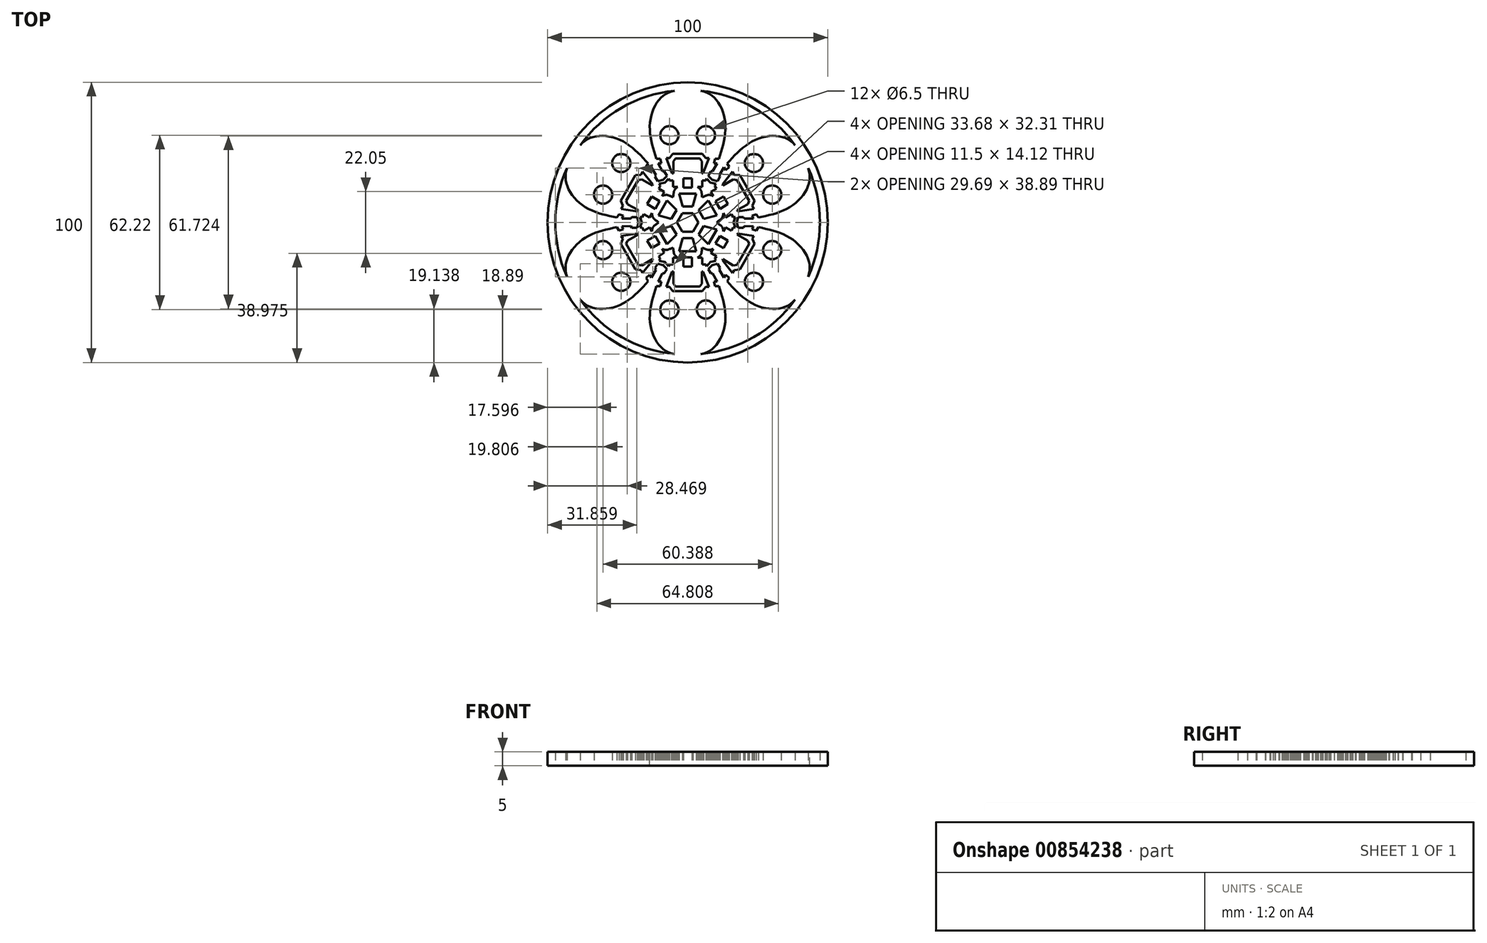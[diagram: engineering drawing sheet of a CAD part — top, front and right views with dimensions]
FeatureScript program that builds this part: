
annotation { "Feature Type Name" : "Feature", "Feature Type Description" : "" }
export const myFeature = defineFeature(function(context is Context, id is Id, definition is map)
    precondition{}
    {
        {
            var Q0;
            Q0=qCreatedBy(makeId("Top.planeOp"),FACE);
            var sketch = newSketch(context, id + "F0", { "sketchPlane" : qUnion([Q0])});
            skLineSegment(sketch, "E0", {"start": v(0, 0) * mm, "end": v(0, 50) * mm});
            skLineSegment(sketch, "E1.1.0", {"start": v(0, 0) * mm, "end": v(-25, 43.3) * mm});
            skLineSegment(sketch, "E1.2.0", {"start": v(0, 0) * mm, "end": v(-43.3, 25) * mm});
            skLineSegment(sketch, "E1.3.0", {"start": v(0, 0) * mm, "end": v(-50, 0) * mm});
            skLineSegment(sketch, "E1.4.0", {"start": v(0, 0) * mm, "end": v(-43.3, -25) * mm});
            skLineSegment(sketch, "E1.5.0", {"start": v(0, 0) * mm, "end": v(-25, -43.3) * mm});
            skLineSegment(sketch, "E1.6.0", {"start": v(0, 0) * mm, "end": v(0, -50) * mm});
            skLineSegment(sketch, "E1.7.0", {"start": v(0, 0) * mm, "end": v(25, -43.3) * mm});
            skLineSegment(sketch, "E1.8.0", {"start": v(0, 0) * mm, "end": v(43.3, -25) * mm});
            skLineSegment(sketch, "E1.9.0", {"start": v(0, 0) * mm, "end": v(50, 0) * mm});
            skLineSegment(sketch, "E1.10.0", {"start": v(0, 0) * mm, "end": v(43.3, 25) * mm});
            skLineSegment(sketch, "E1.11.0", {"start": v(0, 0) * mm, "end": v(25, 43.3) * mm});
            skPoint(sketch, "E1.center", {"position": v(0, 0) * mm});
            skFitSpline(sketch, "E2", {"points": [v(0, 47.42) * mm, v(-9.45, 44.59) * mm, v(-13.5, 34.9) * mm, v(-11.14, 22.73) * mm], "startDerivative": vector(-39.84, 0.36) * mm, "endDerivative": vector(11.08, -33.07) * mm});
            skLineSegment(sketch, "E3", {"start": v(-11.14, 22.73) * mm, "end": v(-9.73, 22.73) * mm});
            skLineSegment(sketch, "E4", {"start": v(-9.73, 22.73) * mm, "end": v(-9.36, 21.09) * mm});
            skLineSegment(sketch, "E5", {"start": v(-9.36, 21.09) * mm, "end": v(-10.54, 21.09) * mm});
            skLineSegment(sketch, "E6", {"start": v(-10.54, 21.09) * mm, "end": v(-8.96, 18.21) * mm});
            skLineSegment(sketch, "E7", {"start": v(-8.96, 18.21) * mm, "end": v(-8.32, 18.21) * mm});
            skLineSegment(sketch, "E8", {"start": v(-8.32, 18.21) * mm, "end": v(-7.4, 16.6) * mm});
            skCircle(sketch, "E9", {"center": v(-6.5, 31.1) * mm, "radius": 3.25 * mm});
            skLineSegment(sketch, "E10", {"start": v(-7.4, 16.6) * mm, "end": v(-8.78, 15.2) * mm});
            skLineSegment(sketch, "E11", {"start": v(-8.18, 14.16) * mm, "end": v(-6.89, 15.63) * mm});
            skLineSegment(sketch, "E12", {"start": v(-6.89, 15.63) * mm, "end": v(-6.5, 14.97) * mm});
            skLineSegment(sketch, "E13", {"start": v(-6.5, 14.97) * mm, "end": v(-5.25, 14.97) * mm});
            skLineSegment(sketch, "E14", {"start": v(-5.25, 14.97) * mm, "end": v(-5.25, 12.64) * mm});
            skLineSegment(sketch, "E15", {"start": v(-5.25, 12.64) * mm, "end": v(-3.55, 12.64) * mm});
            skPoint(sketch, "E16.2.internal.snap0", {"position": v(-5.25, 13.8) * mm});
            skLineSegment(sketch, "E17", {"start": v(-1.89, 3.27) * mm, "end": v(0, 3.27) * mm});
            skLineSegment(sketch, "E18", {"start": v(0, 5.63) * mm, "end": v(-1.8, 5.63) * mm});
            skLineSegment(sketch, "E19", {"start": v(-1.8, 5.63) * mm, "end": v(-3.05, 10.3) * mm});
            skLineSegment(sketch, "E20", {"start": v(-3.05, 10.3) * mm, "end": v(0, 10.3) * mm});
            skFitSpline(sketch, "E21", {"points": [v(-3.55, 12.64) * mm, v(-4.78, 11.36) * mm, v(-5.2, 9) * mm], "startDerivative": vector(-4.82, -3.1) * mm, "endDerivative": vector(-1.27, -9.2) * mm});
            skLineSegment(sketch, "E22", {"start": v(0, 12.43) * mm, "end": v(-1.56, 12.43) * mm});
            skLineSegment(sketch, "E23", {"start": v(-1.56, 12.43) * mm, "end": v(-1.56, 15.75) * mm});
            skLineSegment(sketch, "E24", {"start": v(-1.56, 15.75) * mm, "end": v(0, 15.75) * mm});
            skLineSegment(sketch, "E25", {"start": v(0, 24.54) * mm, "end": v(-5.27, 24.54) * mm});
            skLineSegment(sketch, "E26", {"start": v(-5.27, 24.54) * mm, "end": v(-6.44, 22.95) * mm});
            skLineSegment(sketch, "E27", {"start": v(-6.44, 22.95) * mm, "end": v(-7.63, 22.95) * mm});
            skLineSegment(sketch, "E28", {"start": v(-7.63, 22.95) * mm, "end": v(-5.52, 17.5) * mm});
            skLineSegment(sketch, "E29", {"start": v(-5.52, 17.5) * mm, "end": v(-5.06, 17.5) * mm});
            skLineSegment(sketch, "E30", {"start": v(-5.06, 17.5) * mm, "end": v(-5.13, 21.82) * mm});
            skLineSegment(sketch, "E31", {"start": v(-5.13, 21.82) * mm, "end": v(-4.3, 22.84) * mm});
            skLineSegment(sketch, "E32", {"start": v(-4.3, 22.84) * mm, "end": v(0, 22.84) * mm});
            skLineSegment(sketch, "E33.MirrorCS", {"start": v(6.5, 14.97) * mm, "end": v(5.25, 14.97) * mm});
            skLineSegment(sketch, "E34.MirrorCS", {"start": v(5.25, 14.97) * mm, "end": v(5.25, 12.64) * mm});
            skLineSegment(sketch, "E35.MirrorCS", {"start": v(5.25, 12.64) * mm, "end": v(3.55, 12.64) * mm});
            skLineSegment(sketch, "E36.MirrorCS", {"start": v(9.36, 21.09) * mm, "end": v(10.54, 21.09) * mm});
            skLineSegment(sketch, "E37.MirrorCS", {"start": v(10.54, 21.09) * mm, "end": v(8.96, 18.21) * mm});
            skLineSegment(sketch, "E38.MirrorCS", {"start": v(6.89, 15.63) * mm, "end": v(6.5, 14.97) * mm});
            skLineSegment(sketch, "E39.MirrorCS", {"start": v(8.96, 18.21) * mm, "end": v(8.32, 18.21) * mm});
            skLineSegment(sketch, "E40.MirrorCS", {"start": v(8.32, 18.21) * mm, "end": v(7.4, 16.6) * mm});
            skLineSegment(sketch, "E41.MirrorCS", {"start": v(7.4, 16.6) * mm, "end": v(8.78, 15.2) * mm});
            skFitSpline(sketch, "E42.MirrorCS", {"points": [v(3.55, 12.64) * mm, v(4.78, 11.36) * mm, v(5.2, 9) * mm], "startDerivative": vector(4.82, -3.1) * mm, "endDerivative": vector(1.27, -9.2) * mm});
            skLineSegment(sketch, "E43.MirrorCS", {"start": v(6.44, 22.95) * mm, "end": v(7.63, 22.95) * mm});
            skLineSegment(sketch, "E44.MirrorCS", {"start": v(5.52, 17.5) * mm, "end": v(5.06, 17.5) * mm});
            skLineSegment(sketch, "E45.MirrorCS", {"start": v(11.14, 22.73) * mm, "end": v(9.73, 22.73) * mm});
            skLineSegment(sketch, "E46.MirrorCS", {"start": v(8.18, 14.16) * mm, "end": v(6.89, 15.63) * mm});
            skLineSegment(sketch, "E47.MirrorCS", {"start": v(9.73, 22.73) * mm, "end": v(9.36, 21.09) * mm});
            skLineSegment(sketch, "E48.MirrorCS", {"start": v(5.27, 24.54) * mm, "end": v(6.44, 22.95) * mm});
            skLineSegment(sketch, "E49.MirrorCS", {"start": v(1.8, 5.63) * mm, "end": v(3.05, 10.3) * mm});
            skLineSegment(sketch, "E50.MirrorCS", {"start": v(5.06, 17.5) * mm, "end": v(5.13, 21.82) * mm});
            skLineSegment(sketch, "E51.MirrorCS", {"start": v(7.63, 22.95) * mm, "end": v(5.52, 17.5) * mm});
            skLineSegment(sketch, "E52.MirrorCS", {"start": v(5.13, 21.82) * mm, "end": v(4.3, 22.84) * mm});
            skLineSegment(sketch, "E53.MirrorCS", {"start": v(1.56, 12.43) * mm, "end": v(1.56, 15.75) * mm});
            skPoint(sketch, "E54.MirrorP", {"position": v(5.25, 13.8) * mm});
            skCircle(sketch, "E55.MirrorC", {"center": v(6.5, 31.1) * mm, "radius": 3.25 * mm});
            skFitSpline(sketch, "E56.MirrorCS", {"points": [v(0, 47.42) * mm, v(9.45, 44.59) * mm, v(13.5, 34.9) * mm, v(11.14, 22.73) * mm], "startDerivative": vector(39.84, 0.36) * mm, "endDerivative": vector(-11.08, -33.07) * mm});
            skLineSegment(sketch, "E57.MirrorCS", {"start": v(0, 24.54) * mm, "end": v(5.27, 24.54) * mm});
            skLineSegment(sketch, "E58.MirrorCS", {"start": v(4.3, 22.84) * mm, "end": v(0, 22.84) * mm});
            skLineSegment(sketch, "E59.MirrorCS", {"start": v(1.56, 15.75) * mm, "end": v(0, 15.75) * mm});
            skLineSegment(sketch, "E60.MirrorCS", {"start": v(0, 12.43) * mm, "end": v(1.56, 12.43) * mm});
            skLineSegment(sketch, "E61.MirrorCS", {"start": v(3.05, 10.3) * mm, "end": v(0, 10.3) * mm});
            skLineSegment(sketch, "E62.MirrorCS", {"start": v(0, 5.63) * mm, "end": v(1.8, 5.63) * mm});
            skLineSegment(sketch, "E63.MirrorCS", {"start": v(1.89, 3.27) * mm, "end": v(0, 3.27) * mm});
            skLineSegment(sketch, "E64.MirrorCS", {"start": v(13.58, 1.77) * mm, "end": v(12.72, 3.25) * mm});
            skLineSegment(sketch, "E65.MirrorCS", {"start": v(8.32, 10.87) * mm, "end": v(9.18, 9.4) * mm});
            skLineSegment(sketch, "E66.MirrorCS", {"start": v(12.4, 13.53) * mm, "end": v(12.62, 13.13) * mm});
            skLineSegment(sketch, "E67.MirrorCS", {"start": v(10.76, 6.22) * mm, "end": v(9.98, 7.57) * mm});
            skFitSpline(sketch, "E68.MirrorCS", {"points": [v(9.18, 9.4) * mm, v(7.45, 9.82) * mm, v(5.2, 9) * mm], "startDerivative": vector(-5.1, 2.62) * mm, "endDerivative": vector(-8.6, -3.5) * mm});
            skLineSegment(sketch, "E69.MirrorCS", {"start": v(14.82, 19.8) * mm, "end": v(13.59, 18.65) * mm});
            skLineSegment(sketch, "E70.MirrorCS", {"start": v(15.59, 2.93) * mm, "end": v(13.58, 1.77) * mm});
            skLineSegment(sketch, "E71.MirrorCS", {"start": v(22.94, 2.44) * mm, "end": v(23.53, 1.42) * mm});
            skFitSpline(sketch, "E72.MirrorCS", {"points": [v(12.72, 3.25) * mm, v(12.23, 1.54) * mm, v(10.39, 0) * mm], "startDerivative": vector(-0.27, -5.72) * mm, "endDerivative": vector(-7.33, -5.7) * mm});
            skLineSegment(sketch, "E73.MirrorCS", {"start": v(16.21, 1.85) * mm, "end": v(15.59, 2.93) * mm});
            skLineSegment(sketch, "E74.MirrorCS", {"start": v(16.98, 1.85) * mm, "end": v(16.21, 1.85) * mm});
            skLineSegment(sketch, "E75.MirrorCS", {"start": v(14.12, 21.01) * mm, "end": v(14.82, 19.8) * mm});
            skLineSegment(sketch, "E76.MirrorCS", {"start": v(13.59, 18.65) * mm, "end": v(13, 19.67) * mm});
            skLineSegment(sketch, "E77.MirrorCS", {"start": v(25.25, 1.72) * mm, "end": v(24.55, 2.94) * mm});
            skLineSegment(sketch, "E78.MirrorCS", {"start": v(10.76, 6.22) * mm, "end": v(11.55, 4.86) * mm});
            skLineSegment(sketch, "E79.MirrorCS", {"start": v(17.91, 3.97) * mm, "end": v(17.68, 4.37) * mm});
            skLineSegment(sketch, "E80.MirrorCS", {"start": v(24.55, 2.94) * mm, "end": v(22.94, 2.44) * mm});
            skLineSegment(sketch, "E81.MirrorCS", {"start": v(13, 19.67) * mm, "end": v(11.3, 16.86) * mm});
            skLineSegment(sketch, "E82.MirrorCS", {"start": v(17.68, 4.37) * mm, "end": v(21.46, 6.46) * mm});
            skLineSegment(sketch, "E83.MirrorCS", {"start": v(10.45, 2.5) * mm, "end": v(8.92, 5.15) * mm});
            skLineSegment(sketch, "E84.MirrorCS", {"start": v(11.55, 4.86) * mm, "end": v(14.42, 6.52) * mm});
            skLineSegment(sketch, "E85.MirrorCS", {"start": v(4.88, 2.81) * mm, "end": v(5.78, 1.25) * mm});
            skLineSegment(sketch, "E86.MirrorCS", {"start": v(19.93, 1.9) * mm, "end": v(18.08, 1.9) * mm});
            skLineSegment(sketch, "E87.MirrorCS", {"start": v(23.1, 5.9) * mm, "end": v(23.69, 4.87) * mm});
            skLineSegment(sketch, "E88.MirrorCS", {"start": v(21.46, 6.46) * mm, "end": v(21.93, 7.7) * mm});
            skLineSegment(sketch, "E89.MirrorCS", {"start": v(16.35, 0) * mm, "end": v(16.98, 1.85) * mm});
            skLineSegment(sketch, "E90.MirrorCS", {"start": v(12.86, 9.23) * mm, "end": v(13.64, 7.88) * mm});
            skLineSegment(sketch, "E91.MirrorCS", {"start": v(11.61, 16.31) * mm, "end": v(10.69, 14.7) * mm});
            skLineSegment(sketch, "E92.MirrorCS", {"start": v(10.1, 13.78) * mm, "end": v(9.7, 13.12) * mm});
            skLineSegment(sketch, "E93.MirrorCS", {"start": v(14.42, 6.52) * mm, "end": v(13.64, 7.88) * mm});
            skLineSegment(sketch, "E94.MirrorCS", {"start": v(7.4, 7.8) * mm, "end": v(8.92, 5.15) * mm});
            skLineSegment(sketch, "E95.MirrorCS", {"start": v(9.98, 7.57) * mm, "end": v(12.86, 9.23) * mm});
            skLineSegment(sketch, "E96.MirrorCS", {"start": v(9.7, 13.12) * mm, "end": v(10.33, 12.03) * mm});
            skLineSegment(sketch, "E97.MirrorCS", {"start": v(4.88, 2.81) * mm, "end": v(3.97, 4.38) * mm});
            skLineSegment(sketch, "E98.MirrorCS", {"start": v(10.69, 14.7) * mm, "end": v(8.78, 15.2) * mm});
            skLineSegment(sketch, "E99.MirrorCS", {"start": v(21.25, 12.27) * mm, "end": v(23.89, 7.7) * mm});
            skLineSegment(sketch, "E100.MirrorCS", {"start": v(18.62, 16.84) * mm, "end": v(16.65, 17.05) * mm});
            skLineSegment(sketch, "E101.MirrorCS", {"start": v(16.06, 18.08) * mm, "end": v(12.4, 13.53) * mm});
            skLineSegment(sketch, "E102.MirrorCS", {"start": v(23.53, 1.42) * mm, "end": v(20.25, 1.35) * mm});
            skLineSegment(sketch, "E103.MirrorCS", {"start": v(16.33, 15.35) * mm, "end": v(17.64, 15.14) * mm});
            skLineSegment(sketch, "E104.MirrorCS", {"start": v(20.25, 1.35) * mm, "end": v(19.93, 1.9) * mm});
            skLineSegment(sketch, "E105.MirrorCS", {"start": v(23.89, 7.7) * mm, "end": v(23.1, 5.9) * mm});
            skLineSegment(sketch, "E106.MirrorCS", {"start": v(11.3, 16.86) * mm, "end": v(11.61, 16.31) * mm});
            skLineSegment(sketch, "E107.MirrorCS", {"start": v(8.18, 14.16) * mm, "end": v(10.1, 13.78) * mm});
            skLineSegment(sketch, "E108.MirrorCS", {"start": v(21.93, 7.7) * mm, "end": v(19.78, 11.42) * mm});
            skLineSegment(sketch, "E109.MirrorCS", {"start": v(12.62, 13.13) * mm, "end": v(16.33, 15.35) * mm});
            skLineSegment(sketch, "E110.MirrorCS", {"start": v(18.08, 1.9) * mm, "end": v(17.56, 0) * mm});
            skLineSegment(sketch, "E111.MirrorCS", {"start": v(10.33, 12.03) * mm, "end": v(8.32, 10.87) * mm});
            skLineSegment(sketch, "E112.MirrorCS", {"start": v(16.65, 17.05) * mm, "end": v(16.06, 18.08) * mm});
            skLineSegment(sketch, "E113.MirrorCS", {"start": v(3.77, 0) * mm, "end": v(2.83, 1.63) * mm});
            skLineSegment(sketch, "E114.MirrorCS", {"start": v(3.97, 4.38) * mm, "end": v(7.4, 7.8) * mm});
            skLineSegment(sketch, "E115.MirrorCS", {"start": v(1.89, 3.27) * mm, "end": v(2.83, 1.63) * mm});
            skLineSegment(sketch, "E116.MirrorCS", {"start": v(5.78, 1.25) * mm, "end": v(10.45, 2.5) * mm});
            skFitSpline(sketch, "E117.MirrorCS", {"points": [v(41.07, 23.71) * mm, v(43.34, 14.1) * mm, v(36.97, 5.76) * mm, v(25.25, 1.72) * mm], "startDerivative": vector(20.23, -34.33) * mm, "endDerivative": vector(-34.18, -6.94) * mm});
            skPoint(sketch, "E118.MirrorP", {"position": v(14.58, 2.35) * mm});
            skLineSegment(sketch, "E119.MirrorCS", {"start": v(21.25, 12.27) * mm, "end": v(18.62, 16.84) * mm});
            skPoint(sketch, "E120.MirrorP", {"position": v(9.33, 11.45) * mm});
            skLineSegment(sketch, "E121.MirrorCS", {"start": v(17.64, 15.14) * mm, "end": v(19.78, 11.42) * mm});
            skCircle(sketch, "E122.MirrorC", {"center": v(30.2, 9.92) * mm, "radius": 3.25 * mm});
            skLineSegment(sketch, "E123.MirrorCS", {"start": v(23.69, 4.87) * mm, "end": v(17.91, 3.97) * mm});
            skFitSpline(sketch, "E124.MirrorCS", {"points": [v(41.07, 23.71) * mm, v(33.89, 30.48) * mm, v(23.48, 29.14) * mm, v(14.12, 21.01) * mm], "startDerivative": vector(-19.61, 34.68) * mm, "endDerivative": vector(-23.1, -26.13) * mm});
            skCircle(sketch, "E125.MirrorC", {"center": v(23.69, 21.19) * mm, "radius": 3.25 * mm});
            skLineSegment(sketch, "E126.MirrorCS", {"start": v(-8.32, 10.87) * mm, "end": v(-9.18, 9.4) * mm});
            skLineSegment(sketch, "E127.MirrorCS", {"start": v(-19.93, -1.9) * mm, "end": v(-18.08, -1.9) * mm});
            skLineSegment(sketch, "E128.MirrorCS", {"start": v(-12.4, 13.53) * mm, "end": v(-12.62, 13.13) * mm});
            skLineSegment(sketch, "E129.MirrorCS", {"start": v(-8.32, -10.87) * mm, "end": v(-9.18, -9.4) * mm});
            skFitSpline(sketch, "E130.MirrorCS", {"points": [v(-12.72, -3.25) * mm, v(-12.23, -1.54) * mm, v(-10.39, 0) * mm], "startDerivative": vector(0.27, 5.72) * mm, "endDerivative": vector(7.33, 5.7) * mm});
            skLineSegment(sketch, "E131.MirrorCS", {"start": v(-13.58, 1.77) * mm, "end": v(-12.72, 3.25) * mm});
            skLineSegment(sketch, "E132.MirrorCS", {"start": v(-20.25, -1.35) * mm, "end": v(-19.93, -1.9) * mm});
            skFitSpline(sketch, "E133.MirrorCS", {"points": [v(-12.72, 3.25) * mm, v(-12.23, 1.54) * mm, v(-10.39, 0) * mm], "startDerivative": vector(0.27, -5.72) * mm, "endDerivative": vector(7.33, -5.7) * mm});
            skLineSegment(sketch, "E134.MirrorCS", {"start": v(-13.58, -1.77) * mm, "end": v(-12.72, -3.25) * mm});
            skLineSegment(sketch, "E135.MirrorCS", {"start": v(-16.98, -1.85) * mm, "end": v(-16.21, -1.85) * mm});
            skLineSegment(sketch, "E136.MirrorCS", {"start": v(-10.76, 6.22) * mm, "end": v(-11.55, 4.86) * mm});
            skLineSegment(sketch, "E137.MirrorCS", {"start": v(-10.1, -13.78) * mm, "end": v(-9.7, -13.12) * mm});
            skLineSegment(sketch, "E138.MirrorCS", {"start": v(-16.21, -1.85) * mm, "end": v(-15.59, -2.93) * mm});
            skLineSegment(sketch, "E139.MirrorCS", {"start": v(-25.25, -1.72) * mm, "end": v(-24.55, -2.94) * mm});
            skLineSegment(sketch, "E140.MirrorCS", {"start": v(-16.35, 0) * mm, "end": v(-16.98, -1.85) * mm});
            skLineSegment(sketch, "E141.MirrorCS", {"start": v(-18.08, 1.9) * mm, "end": v(-17.56, 0) * mm});
            skLineSegment(sketch, "E142.MirrorCS", {"start": v(-9.7, -13.12) * mm, "end": v(-10.33, -12.03) * mm});
            skLineSegment(sketch, "E143.MirrorCS", {"start": v(-14.12, -21.01) * mm, "end": v(-14.82, -19.8) * mm});
            skLineSegment(sketch, "E144.MirrorCS", {"start": v(-8.18, -14.16) * mm, "end": v(-10.1, -13.78) * mm});
            skFitSpline(sketch, "E145.MirrorCS", {"points": [v(-9.18, -9.4) * mm, v(-7.45, -9.82) * mm, v(-5.2, -9) * mm], "startDerivative": vector(5.1, -2.62) * mm, "endDerivative": vector(8.6, 3.5) * mm});
            skLineSegment(sketch, "E146.MirrorCS", {"start": v(-15.59, -2.93) * mm, "end": v(-13.58, -1.77) * mm});
            skLineSegment(sketch, "E147.MirrorCS", {"start": v(-10.1, 13.78) * mm, "end": v(-9.7, 13.12) * mm});
            skLineSegment(sketch, "E148.MirrorCS", {"start": v(-10.76, 6.22) * mm, "end": v(-9.98, 7.57) * mm});
            skLineSegment(sketch, "E149.MirrorCS", {"start": v(-16.98, 1.85) * mm, "end": v(-16.21, 1.85) * mm});
            skLineSegment(sketch, "E150.MirrorCS", {"start": v(-25.25, 1.72) * mm, "end": v(-24.55, 2.94) * mm});
            skLineSegment(sketch, "E151.MirrorCS", {"start": v(-16.35, 0) * mm, "end": v(-16.98, 1.85) * mm});
            skLineSegment(sketch, "E152.MirrorCS", {"start": v(-18.08, -1.9) * mm, "end": v(-17.56, 0) * mm});
            skLineSegment(sketch, "E153.MirrorCS", {"start": v(-9.7, 13.12) * mm, "end": v(-10.33, 12.03) * mm});
            skLineSegment(sketch, "E154.MirrorCS", {"start": v(-10.33, -12.03) * mm, "end": v(-8.32, -10.87) * mm});
            skLineSegment(sketch, "E155.MirrorCS", {"start": v(-13.59, -18.65) * mm, "end": v(-13, -19.67) * mm});
            skLineSegment(sketch, "E156.MirrorCS", {"start": v(-11.61, -16.31) * mm, "end": v(-10.69, -14.7) * mm});
            skLineSegment(sketch, "E157.MirrorCS", {"start": v(-10.76, -6.22) * mm, "end": v(-11.55, -4.86) * mm});
            skLineSegment(sketch, "E158.MirrorCS", {"start": v(-10.76, -6.22) * mm, "end": v(-9.98, -7.57) * mm});
            skLineSegment(sketch, "E159.MirrorCS", {"start": v(-15.59, 2.93) * mm, "end": v(-13.58, 1.77) * mm});
            skLineSegment(sketch, "E160.MirrorCS", {"start": v(-17.91, 3.97) * mm, "end": v(-17.68, 4.37) * mm});
            skLineSegment(sketch, "E161.MirrorCS", {"start": v(-10.69, -14.7) * mm, "end": v(-8.78, -15.2) * mm});
            skLineSegment(sketch, "E162.MirrorCS", {"start": v(-16.21, 1.85) * mm, "end": v(-15.59, 2.93) * mm});
            skLineSegment(sketch, "E163.MirrorCS", {"start": v(-8.18, 14.16) * mm, "end": v(-10.1, 13.78) * mm});
            skLineSegment(sketch, "E164.MirrorCS", {"start": v(-14.12, 21.01) * mm, "end": v(-14.82, 19.8) * mm});
            skFitSpline(sketch, "E165.MirrorCS", {"points": [v(-9.18, 9.4) * mm, v(-7.45, 9.82) * mm, v(-5.2, 9) * mm], "startDerivative": vector(5.1, 2.62) * mm, "endDerivative": vector(8.6, -3.5) * mm});
            skLineSegment(sketch, "E166.MirrorCS", {"start": v(-3.77, 0) * mm, "end": v(-2.83, -1.63) * mm});
            skLineSegment(sketch, "E167.MirrorCS", {"start": v(-1.89, -3.27) * mm, "end": v(-2.83, -1.63) * mm});
            skLineSegment(sketch, "E168.MirrorCS", {"start": v(-10.33, 12.03) * mm, "end": v(-8.32, 10.87) * mm});
            skLineSegment(sketch, "E169.MirrorCS", {"start": v(-13.59, 18.65) * mm, "end": v(-13, 19.67) * mm});
            skLineSegment(sketch, "E170.MirrorCS", {"start": v(-23.1, -5.9) * mm, "end": v(-23.69, -4.87) * mm});
            skLineSegment(sketch, "E171.MirrorCS", {"start": v(-14.42, 6.52) * mm, "end": v(-13.64, 7.88) * mm});
            skLineSegment(sketch, "E172.MirrorCS", {"start": v(-11.3, 16.86) * mm, "end": v(-11.61, 16.31) * mm});
            skLineSegment(sketch, "E173.MirrorCS", {"start": v(-10.45, 2.5) * mm, "end": v(-8.92, 5.15) * mm});
            skLineSegment(sketch, "E174.MirrorCS", {"start": v(-12.86, -9.23) * mm, "end": v(-13.64, -7.88) * mm});
            skLineSegment(sketch, "E175.MirrorCS", {"start": v(-17.68, -4.37) * mm, "end": v(-21.46, -6.46) * mm});
            skLineSegment(sketch, "E176.MirrorCS", {"start": v(-18.62, -16.84) * mm, "end": v(-16.65, -17.05) * mm});
            skLineSegment(sketch, "E177.MirrorCS", {"start": v(-10.69, 14.7) * mm, "end": v(-8.78, 15.2) * mm});
            skLineSegment(sketch, "E178.MirrorCS", {"start": v(-16.65, 17.05) * mm, "end": v(-16.06, 18.08) * mm});
            skLineSegment(sketch, "E179.MirrorCS", {"start": v(-9.98, 7.57) * mm, "end": v(-12.86, 9.23) * mm});
            skLineSegment(sketch, "E180.MirrorCS", {"start": v(-23.1, 5.9) * mm, "end": v(-23.69, 4.87) * mm});
            skLineSegment(sketch, "E181.MirrorCS", {"start": v(-20.25, 1.35) * mm, "end": v(-19.93, 1.9) * mm});
            skLineSegment(sketch, "E182.MirrorCS", {"start": v(-3.77, 0) * mm, "end": v(-2.83, 1.63) * mm});
            skLineSegment(sketch, "E183.MirrorCS", {"start": v(-12.4, -13.53) * mm, "end": v(-12.62, -13.13) * mm});
            skLineSegment(sketch, "E184.MirrorCS", {"start": v(-11.55, -4.86) * mm, "end": v(-14.42, -6.52) * mm});
            skLineSegment(sketch, "E185.MirrorCS", {"start": v(-16.33, -15.35) * mm, "end": v(-17.64, -15.14) * mm});
            skLineSegment(sketch, "E186.MirrorCS", {"start": v(-11.3, -16.86) * mm, "end": v(-11.61, -16.31) * mm});
            skLineSegment(sketch, "E187.MirrorCS", {"start": v(-14.82, -19.8) * mm, "end": v(-13.59, -18.65) * mm});
            skLineSegment(sketch, "E188.MirrorCS", {"start": v(-5.78, -1.25) * mm, "end": v(-10.45, -2.5) * mm});
            skLineSegment(sketch, "E189.MirrorCS", {"start": v(-14.82, 19.8) * mm, "end": v(-13.59, 18.65) * mm});
            skLineSegment(sketch, "E190.MirrorCS", {"start": v(-23.89, 7.7) * mm, "end": v(-23.1, 5.9) * mm});
            skLineSegment(sketch, "E191.MirrorCS", {"start": v(-18.62, 16.84) * mm, "end": v(-16.65, 17.05) * mm});
            skLineSegment(sketch, "E192.MirrorCS", {"start": v(-21.93, 7.7) * mm, "end": v(-19.78, 11.42) * mm});
            skLineSegment(sketch, "E193.MirrorCS", {"start": v(-7.4, 7.8) * mm, "end": v(-8.92, 5.15) * mm});
            skLineSegment(sketch, "E194.MirrorCS", {"start": v(-12.62, -13.13) * mm, "end": v(-16.33, -15.35) * mm});
            skLineSegment(sketch, "E195.MirrorCS", {"start": v(-19.93, 1.9) * mm, "end": v(-18.08, 1.9) * mm});
            skLineSegment(sketch, "E196.MirrorCS", {"start": v(-11.55, 4.86) * mm, "end": v(-14.42, 6.52) * mm});
            skLineSegment(sketch, "E197.MirrorCS", {"start": v(-4.88, 2.81) * mm, "end": v(-5.78, 1.25) * mm});
            skLineSegment(sketch, "E198.MirrorCS", {"start": v(-21.25, -12.27) * mm, "end": v(-23.89, -7.7) * mm});
            skLineSegment(sketch, "E199.MirrorCS", {"start": v(-14.42, -6.52) * mm, "end": v(-13.64, -7.88) * mm});
            skLineSegment(sketch, "E200.MirrorCS", {"start": v(-21.46, 6.46) * mm, "end": v(-21.93, 7.7) * mm});
            skLineSegment(sketch, "E201.MirrorCS", {"start": v(-1.89, 3.27) * mm, "end": v(-2.83, 1.63) * mm});
            skLineSegment(sketch, "E202.MirrorCS", {"start": v(-11.61, 16.31) * mm, "end": v(-10.69, 14.7) * mm});
            skLineSegment(sketch, "E203.MirrorCS", {"start": v(-24.55, -2.94) * mm, "end": v(-22.94, -2.44) * mm});
            skLineSegment(sketch, "E204.MirrorCS", {"start": v(-12.86, 9.23) * mm, "end": v(-13.64, 7.88) * mm});
            skLineSegment(sketch, "E205.MirrorCS", {"start": v(-23.53, 1.42) * mm, "end": v(-20.25, 1.35) * mm});
            skLineSegment(sketch, "E206.MirrorCS", {"start": v(-21.93, -7.7) * mm, "end": v(-19.78, -11.42) * mm});
            skLineSegment(sketch, "E207.MirrorCS", {"start": v(-24.55, 2.94) * mm, "end": v(-22.94, 2.44) * mm});
            skLineSegment(sketch, "E208.MirrorCS", {"start": v(-4.88, -2.81) * mm, "end": v(-3.97, -4.38) * mm});
            skLineSegment(sketch, "E209.MirrorCS", {"start": v(-22.94, 2.44) * mm, "end": v(-23.53, 1.42) * mm});
            skLineSegment(sketch, "E210.MirrorCS", {"start": v(-4.88, -2.81) * mm, "end": v(-5.78, -1.25) * mm});
            skLineSegment(sketch, "E211.MirrorCS", {"start": v(-10.45, -2.5) * mm, "end": v(-8.92, -5.15) * mm});
            skLineSegment(sketch, "E212.MirrorCS", {"start": v(-16.33, 15.35) * mm, "end": v(-17.64, 15.14) * mm});
            skLineSegment(sketch, "E213.MirrorCS", {"start": v(-9.98, -7.57) * mm, "end": v(-12.86, -9.23) * mm});
            skLineSegment(sketch, "E214.MirrorCS", {"start": v(-23.89, -7.7) * mm, "end": v(-23.1, -5.9) * mm});
            skLineSegment(sketch, "E215.MirrorCS", {"start": v(-4.88, 2.81) * mm, "end": v(-3.97, 4.38) * mm});
            skLineSegment(sketch, "E216.MirrorCS", {"start": v(-17.64, -15.14) * mm, "end": v(-19.78, -11.42) * mm});
            skLineSegment(sketch, "E217.MirrorCS", {"start": v(-23.53, -1.42) * mm, "end": v(-20.25, -1.35) * mm});
            skLineSegment(sketch, "E218.MirrorCS", {"start": v(-7.4, -7.8) * mm, "end": v(-8.92, -5.15) * mm});
            skLineSegment(sketch, "E219.MirrorCS", {"start": v(-13, -19.67) * mm, "end": v(-11.3, -16.86) * mm});
            skLineSegment(sketch, "E220.MirrorCS", {"start": v(-16.65, -17.05) * mm, "end": v(-16.06, -18.08) * mm});
            skLineSegment(sketch, "E221.MirrorCS", {"start": v(-22.94, -2.44) * mm, "end": v(-23.53, -1.42) * mm});
            skLineSegment(sketch, "E222.MirrorCS", {"start": v(-21.46, -6.46) * mm, "end": v(-21.93, -7.7) * mm});
            skLineSegment(sketch, "E223.MirrorCS", {"start": v(-13, 19.67) * mm, "end": v(-11.3, 16.86) * mm});
            skLineSegment(sketch, "E224.MirrorCS", {"start": v(-17.91, -3.97) * mm, "end": v(-17.68, -4.37) * mm});
            skLineSegment(sketch, "E225.MirrorCS", {"start": v(-23.69, 4.87) * mm, "end": v(-17.91, 3.97) * mm});
            skLineSegment(sketch, "E226.MirrorCS", {"start": v(-3.97, 4.38) * mm, "end": v(-7.4, 7.8) * mm});
            skLineSegment(sketch, "E227.MirrorCS", {"start": v(-3.97, -4.38) * mm, "end": v(-7.4, -7.8) * mm});
            skLineSegment(sketch, "E228.MirrorCS", {"start": v(-5.78, 1.25) * mm, "end": v(-10.45, 2.5) * mm});
            skCircle(sketch, "E229.MirrorC", {"center": v(-30.2, 9.92) * mm, "radius": 3.25 * mm});
            skFitSpline(sketch, "E230.MirrorCS", {"points": [v(-41.07, 23.71) * mm, v(-33.89, 30.48) * mm, v(-23.48, 29.14) * mm, v(-14.12, 21.01) * mm], "startDerivative": vector(19.61, 34.68) * mm, "endDerivative": vector(23.1, -26.13) * mm});
            skCircle(sketch, "E231.MirrorC", {"center": v(-30.2, -9.92) * mm, "radius": 3.25 * mm});
            skLineSegment(sketch, "E232.MirrorCS", {"start": v(-21.25, 12.27) * mm, "end": v(-18.62, 16.84) * mm});
            skPoint(sketch, "E233.MirrorP", {"position": v(-9.33, -11.45) * mm});
            skLineSegment(sketch, "E234.MirrorCS", {"start": v(-21.25, 12.27) * mm, "end": v(-23.89, 7.7) * mm});
            skLineSegment(sketch, "E235.MirrorCS", {"start": v(-16.06, -18.08) * mm, "end": v(-12.4, -13.53) * mm});
            skFitSpline(sketch, "E236.MirrorCS", {"points": [v(-41.07, 23.71) * mm, v(-43.34, 14.1) * mm, v(-36.97, 5.76) * mm, v(-25.25, 1.72) * mm], "startDerivative": vector(-20.23, -34.33) * mm, "endDerivative": vector(34.18, -6.94) * mm});
            skLineSegment(sketch, "E237.MirrorCS", {"start": v(-12.62, 13.13) * mm, "end": v(-16.33, 15.35) * mm});
            skLineSegment(sketch, "E238.MirrorCS", {"start": v(-17.64, 15.14) * mm, "end": v(-19.78, 11.42) * mm});
            skCircle(sketch, "E239.MirrorC", {"center": v(-23.69, 21.19) * mm, "radius": 3.25 * mm});
            skLineSegment(sketch, "E240.MirrorCS", {"start": v(-21.25, -12.27) * mm, "end": v(-18.62, -16.84) * mm});
            skCircle(sketch, "E241.MirrorC", {"center": v(-23.69, -21.19) * mm, "radius": 3.25 * mm});
            skPoint(sketch, "E242.MirrorP", {"position": v(-14.58, -2.35) * mm});
            skPoint(sketch, "E243.MirrorP", {"position": v(-9.33, 11.45) * mm});
            skPoint(sketch, "E244.MirrorP", {"position": v(-14.58, 2.35) * mm});
            skLineSegment(sketch, "E245.MirrorCS", {"start": v(-17.68, 4.37) * mm, "end": v(-21.46, 6.46) * mm});
            skLineSegment(sketch, "E246.MirrorCS", {"start": v(-16.06, 18.08) * mm, "end": v(-12.4, 13.53) * mm});
            skLineSegment(sketch, "E247.MirrorCS", {"start": v(-23.69, -4.87) * mm, "end": v(-17.91, -3.97) * mm});
            skFitSpline(sketch, "E248.MirrorCS", {"points": [v(-41.07, -23.71) * mm, v(-33.89, -30.48) * mm, v(-23.48, -29.14) * mm, v(-14.12, -21.01) * mm], "startDerivative": vector(19.61, -34.68) * mm, "endDerivative": vector(23.1, 26.13) * mm});
            skFitSpline(sketch, "E249.MirrorCS", {"points": [v(-41.07, -23.71) * mm, v(-43.34, -14.1) * mm, v(-36.97, -5.76) * mm, v(-25.25, -1.72) * mm], "startDerivative": vector(-20.23, 34.33) * mm, "endDerivative": vector(34.18, 6.94) * mm});
            skLineSegment(sketch, "E250.MirrorCS", {"start": v(16.21, -1.85) * mm, "end": v(15.59, -2.93) * mm});
            skLineSegment(sketch, "E251.MirrorCS", {"start": v(10.1, -13.78) * mm, "end": v(9.7, -13.12) * mm});
            skLineSegment(sketch, "E252.MirrorCS", {"start": v(16.98, -1.85) * mm, "end": v(16.21, -1.85) * mm});
            skLineSegment(sketch, "E253.MirrorCS", {"start": v(-5.13, -21.82) * mm, "end": v(-4.3, -22.84) * mm});
            skLineSegment(sketch, "E254.MirrorCS", {"start": v(8.32, -10.87) * mm, "end": v(9.18, -9.4) * mm});
            skLineSegment(sketch, "E255.MirrorCS", {"start": v(15.59, -2.93) * mm, "end": v(13.58, -1.77) * mm});
            skLineSegment(sketch, "E256.MirrorCS", {"start": v(-7.4, -16.6) * mm, "end": v(-8.78, -15.2) * mm});
            skLineSegment(sketch, "E257.MirrorCS", {"start": v(8.18, -14.16) * mm, "end": v(6.89, -15.63) * mm});
            skLineSegment(sketch, "E258.MirrorCS", {"start": v(5.25, -12.64) * mm, "end": v(3.55, -12.64) * mm});
            skLineSegment(sketch, "E259.MirrorCS", {"start": v(-6.44, -22.95) * mm, "end": v(-7.63, -22.95) * mm});
            skLineSegment(sketch, "E260.MirrorCS", {"start": v(-9.73, -22.73) * mm, "end": v(-9.36, -21.09) * mm});
            skLineSegment(sketch, "E261.MirrorCS", {"start": v(-8.18, -14.16) * mm, "end": v(-6.89, -15.63) * mm});
            skLineSegment(sketch, "E262.MirrorCS", {"start": v(-5.25, -12.64) * mm, "end": v(-3.55, -12.64) * mm});
            skLineSegment(sketch, "E263.MirrorCS", {"start": v(13.58, -1.77) * mm, "end": v(12.72, -3.25) * mm});
            skFitSpline(sketch, "E264.MirrorCS", {"points": [v(3.55, -12.64) * mm, v(4.78, -11.36) * mm, v(5.2, -9) * mm], "startDerivative": vector(4.82, 3.1) * mm, "endDerivative": vector(1.27, 9.2) * mm});
            skFitSpline(sketch, "E265.MirrorCS", {"points": [v(-3.55, -12.64) * mm, v(-4.78, -11.36) * mm, v(-5.2, -9) * mm], "startDerivative": vector(-4.82, 3.1) * mm, "endDerivative": vector(-1.27, 9.2) * mm});
            skLineSegment(sketch, "E266.MirrorCS", {"start": v(6.5, -14.97) * mm, "end": v(5.25, -14.97) * mm});
            skLineSegment(sketch, "E267.MirrorCS", {"start": v(-8.96, -18.21) * mm, "end": v(-8.32, -18.21) * mm});
            skLineSegment(sketch, "E268.MirrorCS", {"start": v(5.52, -17.5) * mm, "end": v(5.06, -17.5) * mm});
            skLineSegment(sketch, "E269.MirrorCS", {"start": v(17.91, -3.97) * mm, "end": v(17.68, -4.37) * mm});
            skLineSegment(sketch, "E270.MirrorCS", {"start": v(-5.27, -24.54) * mm, "end": v(-6.44, -22.95) * mm});
            skLineSegment(sketch, "E271.MirrorCS", {"start": v(-8.32, -18.21) * mm, "end": v(-7.4, -16.6) * mm});
            skLineSegment(sketch, "E272.MirrorCS", {"start": v(12.4, -13.53) * mm, "end": v(12.62, -13.13) * mm});
            skLineSegment(sketch, "E273.MirrorCS", {"start": v(10.33, -12.03) * mm, "end": v(8.32, -10.87) * mm});
            skLineSegment(sketch, "E274.MirrorCS", {"start": v(8.18, -14.16) * mm, "end": v(10.1, -13.78) * mm});
            skLineSegment(sketch, "E275.MirrorCS", {"start": v(-6.5, -14.97) * mm, "end": v(-5.25, -14.97) * mm});
            skFitSpline(sketch, "E276.MirrorCS", {"points": [v(9.18, -9.4) * mm, v(7.45, -9.82) * mm, v(5.2, -9) * mm], "startDerivative": vector(-5.1, -2.62) * mm, "endDerivative": vector(-8.6, 3.5) * mm});
            skLineSegment(sketch, "E277.MirrorCS", {"start": v(6.89, -15.63) * mm, "end": v(6.5, -14.97) * mm});
            skLineSegment(sketch, "E278.MirrorCS", {"start": v(5.25, -14.97) * mm, "end": v(5.25, -12.64) * mm});
            skLineSegment(sketch, "E279.MirrorCS", {"start": v(9.7, -13.12) * mm, "end": v(10.33, -12.03) * mm});
            skLineSegment(sketch, "E280.MirrorCS", {"start": v(-6.89, -15.63) * mm, "end": v(-6.5, -14.97) * mm});
            skFitSpline(sketch, "E281.MirrorCS", {"points": [v(-9.18, -9.4) * mm, v(-7.45, -9.82) * mm, v(-5.2, -9) * mm], "startDerivative": vector(5.1, -2.62) * mm, "endDerivative": vector(8.6, 3.5) * mm});
            skLineSegment(sketch, "E282.MirrorCS", {"start": v(-11.14, -22.73) * mm, "end": v(-9.73, -22.73) * mm});
            skLineSegment(sketch, "E283.MirrorCS", {"start": v(6.44, -22.95) * mm, "end": v(7.63, -22.95) * mm});
            skLineSegment(sketch, "E284.MirrorCS", {"start": v(9.73, -22.73) * mm, "end": v(9.36, -21.09) * mm});
            skLineSegment(sketch, "E285.MirrorCS", {"start": v(14.82, -19.8) * mm, "end": v(13.59, -18.65) * mm});
            skLineSegment(sketch, "E286.MirrorCS", {"start": v(-5.52, -17.5) * mm, "end": v(-5.06, -17.5) * mm});
            skLineSegment(sketch, "E287.MirrorCS", {"start": v(-1.89, -3.27) * mm, "end": v(0, -3.27) * mm});
            skLineSegment(sketch, "E288.MirrorCS", {"start": v(-5.25, -14.97) * mm, "end": v(-5.25, -12.64) * mm});
            skLineSegment(sketch, "E289.MirrorCS", {"start": v(11.3, -16.86) * mm, "end": v(11.61, -16.31) * mm});
            skLineSegment(sketch, "E290.MirrorCS", {"start": v(7.4, -16.6) * mm, "end": v(8.78, -15.2) * mm});
            skLineSegment(sketch, "E291.MirrorCS", {"start": v(16.65, -17.05) * mm, "end": v(16.06, -18.08) * mm});
            skLineSegment(sketch, "E292.MirrorCS", {"start": v(13, -19.67) * mm, "end": v(11.3, -16.86) * mm});
            skLineSegment(sketch, "E293.MirrorCS", {"start": v(19.93, -1.9) * mm, "end": v(18.08, -1.9) * mm});
            skLineSegment(sketch, "E294.MirrorCS", {"start": v(18.62, -16.84) * mm, "end": v(16.65, -17.05) * mm});
            skLineSegment(sketch, "E295.MirrorCS", {"start": v(8.32, -18.21) * mm, "end": v(7.4, -16.6) * mm});
            skLineSegment(sketch, "E296.MirrorCS", {"start": v(5.27, -24.54) * mm, "end": v(6.44, -22.95) * mm});
            skLineSegment(sketch, "E297.MirrorCS", {"start": v(13.59, -18.65) * mm, "end": v(13, -19.67) * mm});
            skLineSegment(sketch, "E298.MirrorCS", {"start": v(8.96, -18.21) * mm, "end": v(8.32, -18.21) * mm});
            skLineSegment(sketch, "E299.MirrorCS", {"start": v(14.12, -21.01) * mm, "end": v(14.82, -19.8) * mm});
            skLineSegment(sketch, "E300.MirrorCS", {"start": v(10.69, -14.7) * mm, "end": v(8.78, -15.2) * mm});
            skLineSegment(sketch, "E301.MirrorCS", {"start": v(-9.36, -21.09) * mm, "end": v(-10.54, -21.09) * mm});
            skLineSegment(sketch, "E302.MirrorCS", {"start": v(0, -12.43) * mm, "end": v(1.56, -12.43) * mm});
            skLineSegment(sketch, "E303.MirrorCS", {"start": v(11.14, -22.73) * mm, "end": v(9.73, -22.73) * mm});
            skLineSegment(sketch, "E304.MirrorCS", {"start": v(16.33, -15.35) * mm, "end": v(17.64, -15.14) * mm});
            skLineSegment(sketch, "E305.MirrorCS", {"start": v(0, -12.43) * mm, "end": v(-1.56, -12.43) * mm});
            skLineSegment(sketch, "E306.MirrorCS", {"start": v(11.55, -4.86) * mm, "end": v(14.42, -6.52) * mm});
            skLineSegment(sketch, "E307.MirrorCS", {"start": v(-5.06, -17.5) * mm, "end": v(-5.13, -21.82) * mm});
            skLineSegment(sketch, "E308.MirrorCS", {"start": v(5.06, -17.5) * mm, "end": v(5.13, -21.82) * mm});
            skLineSegment(sketch, "E309.MirrorCS", {"start": v(10.45, -2.5) * mm, "end": v(8.92, -5.15) * mm});
            skLineSegment(sketch, "E310.MirrorCS", {"start": v(-1.56, -12.43) * mm, "end": v(-1.56, -15.75) * mm});
            skLineSegment(sketch, "E311.MirrorCS", {"start": v(5.13, -21.82) * mm, "end": v(4.3, -22.84) * mm});
            skLineSegment(sketch, "E312.MirrorCS", {"start": v(7.4, -7.8) * mm, "end": v(8.92, -5.15) * mm});
            skLineSegment(sketch, "E313.MirrorCS", {"start": v(12.86, -9.23) * mm, "end": v(13.64, -7.88) * mm});
            skLineSegment(sketch, "E314.MirrorCS", {"start": v(17.68, -4.37) * mm, "end": v(21.46, -6.46) * mm});
            skLineSegment(sketch, "E315.MirrorCS", {"start": v(10.54, -21.09) * mm, "end": v(8.96, -18.21) * mm});
            skLineSegment(sketch, "E316.MirrorCS", {"start": v(1.56, -12.43) * mm, "end": v(1.56, -15.75) * mm});
            skLineSegment(sketch, "E317.MirrorCS", {"start": v(-10.54, -21.09) * mm, "end": v(-8.96, -18.21) * mm});
            skLineSegment(sketch, "E318.MirrorCS", {"start": v(22.94, -2.44) * mm, "end": v(23.53, -1.42) * mm});
            skLineSegment(sketch, "E319.MirrorCS", {"start": v(1.89, -3.27) * mm, "end": v(2.83, -1.63) * mm});
            skLineSegment(sketch, "E320.MirrorCS", {"start": v(10.76, -6.22) * mm, "end": v(11.55, -4.86) * mm});
            skLineSegment(sketch, "E321.MirrorCS", {"start": v(-3.05, -10.3) * mm, "end": v(0, -10.3) * mm});
            skLineSegment(sketch, "E322.MirrorCS", {"start": v(11.61, -16.31) * mm, "end": v(10.69, -14.7) * mm});
            skLineSegment(sketch, "E323.MirrorCS", {"start": v(14.42, -6.52) * mm, "end": v(13.64, -7.88) * mm});
            skLineSegment(sketch, "E324.MirrorCS", {"start": v(4.88, -2.81) * mm, "end": v(3.97, -4.38) * mm});
            skLineSegment(sketch, "E325.MirrorCS", {"start": v(-4.3, -22.84) * mm, "end": v(0, -22.84) * mm});
            skLineSegment(sketch, "E326.MirrorCS", {"start": v(0, -5.63) * mm, "end": v(-1.8, -5.63) * mm});
            skLineSegment(sketch, "E327.MirrorCS", {"start": v(21.46, -6.46) * mm, "end": v(21.93, -7.7) * mm});
            skLineSegment(sketch, "E328.MirrorCS", {"start": v(23.89, -7.7) * mm, "end": v(23.1, -5.9) * mm});
            skLineSegment(sketch, "E329.MirrorCS", {"start": v(10.76, -6.22) * mm, "end": v(9.98, -7.57) * mm});
            skLineSegment(sketch, "E330.MirrorCS", {"start": v(17.64, -15.14) * mm, "end": v(19.78, -11.42) * mm});
            skLineSegment(sketch, "E331.MirrorCS", {"start": v(1.56, -15.75) * mm, "end": v(0, -15.75) * mm});
            skLineSegment(sketch, "E332.MirrorCS", {"start": v(1.89, -3.27) * mm, "end": v(0, -3.27) * mm});
            skLineSegment(sketch, "E333.MirrorCS", {"start": v(25.25, -1.72) * mm, "end": v(24.55, -2.94) * mm});
            skLineSegment(sketch, "E334.MirrorCS", {"start": v(9.98, -7.57) * mm, "end": v(12.86, -9.23) * mm});
            skLineSegment(sketch, "E335.MirrorCS", {"start": v(12.62, -13.13) * mm, "end": v(16.33, -15.35) * mm});
            skLineSegment(sketch, "E336.MirrorCS", {"start": v(21.93, -7.7) * mm, "end": v(19.78, -11.42) * mm});
            skLineSegment(sketch, "E337.MirrorCS", {"start": v(0, -5.63) * mm, "end": v(1.8, -5.63) * mm});
            skLineSegment(sketch, "E338.MirrorCS", {"start": v(-1.56, -15.75) * mm, "end": v(0, -15.75) * mm});
            skLineSegment(sketch, "E339.MirrorCS", {"start": v(7.63, -22.95) * mm, "end": v(5.52, -17.5) * mm});
            skLineSegment(sketch, "E340.MirrorCS", {"start": v(23.1, -5.9) * mm, "end": v(23.69, -4.87) * mm});
            skLineSegment(sketch, "E341.MirrorCS", {"start": v(24.55, -2.94) * mm, "end": v(22.94, -2.44) * mm});
            skLineSegment(sketch, "E342.MirrorCS", {"start": v(3.05, -10.3) * mm, "end": v(0, -10.3) * mm});
            skLineSegment(sketch, "E343.MirrorCS", {"start": v(9.36, -21.09) * mm, "end": v(10.54, -21.09) * mm});
            skLineSegment(sketch, "E344.MirrorCS", {"start": v(-1.8, -5.63) * mm, "end": v(-3.05, -10.3) * mm});
            skLineSegment(sketch, "E345.MirrorCS", {"start": v(1.8, -5.63) * mm, "end": v(3.05, -10.3) * mm});
            skPoint(sketch, "E346.MirrorP", {"position": v(14.58, -2.35) * mm});
            skCircle(sketch, "E347.MirrorC", {"center": v(23.69, -21.19) * mm, "radius": 3.25 * mm});
            skLineSegment(sketch, "E348.MirrorCS", {"start": v(21.25, -12.27) * mm, "end": v(18.62, -16.84) * mm});
            skLineSegment(sketch, "E349.MirrorCS", {"start": v(-7.63, -22.95) * mm, "end": v(-5.52, -17.5) * mm});
            skFitSpline(sketch, "E350.MirrorCS", {"points": [v(41.07, -23.71) * mm, v(33.89, -30.48) * mm, v(23.48, -29.14) * mm, v(14.12, -21.01) * mm], "startDerivative": vector(-19.61, -34.68) * mm, "endDerivative": vector(-23.1, 26.13) * mm});
            skLineSegment(sketch, "E351.MirrorCS", {"start": v(0, -24.54) * mm, "end": v(5.27, -24.54) * mm});
            skLineSegment(sketch, "E352.MirrorCS", {"start": v(21.25, -12.27) * mm, "end": v(23.89, -7.7) * mm});
            skCircle(sketch, "E353.MirrorC", {"center": v(6.5, -31.1) * mm, "radius": 3.25 * mm});
            skCircle(sketch, "E354.MirrorC", {"center": v(30.2, -9.92) * mm, "radius": 3.25 * mm});
            skLineSegment(sketch, "E355.MirrorCS", {"start": v(3.97, -4.38) * mm, "end": v(7.4, -7.8) * mm});
            skPoint(sketch, "E356.MirrorP", {"position": v(-5.25, -13.8) * mm});
            skLineSegment(sketch, "E357.MirrorCS", {"start": v(0, -24.54) * mm, "end": v(-5.27, -24.54) * mm});
            skLineSegment(sketch, "E358.MirrorCS", {"start": v(16.06, -18.08) * mm, "end": v(12.4, -13.53) * mm});
            skPoint(sketch, "E359.MirrorP", {"position": v(5.25, -13.8) * mm});
            skPoint(sketch, "E360.MirrorP", {"position": v(9.33, -11.45) * mm});
            skLineSegment(sketch, "E361.MirrorCS", {"start": v(4.3, -22.84) * mm, "end": v(0, -22.84) * mm});
            skCircle(sketch, "E362.MirrorC", {"center": v(-6.5, -31.1) * mm, "radius": 3.25 * mm});
            skLineSegment(sketch, "E363.MirrorCS", {"start": v(23.69, -4.87) * mm, "end": v(17.91, -3.97) * mm});
            skFitSpline(sketch, "E364.MirrorCS", {"points": [v(0, -47.42) * mm, v(-9.45, -44.59) * mm, v(-13.5, -34.9) * mm, v(-11.14, -22.73) * mm], "startDerivative": vector(-39.84, -0.36) * mm, "endDerivative": vector(11.08, 33.07) * mm});
            skFitSpline(sketch, "E365.MirrorCS", {"points": [v(0, -47.42) * mm, v(9.45, -44.59) * mm, v(13.5, -34.9) * mm, v(11.14, -22.73) * mm], "startDerivative": vector(39.84, -0.36) * mm, "endDerivative": vector(-11.08, 33.07) * mm});
            skFitSpline(sketch, "E366.MirrorCS", {"points": [v(12.72, -3.25) * mm, v(12.23, -1.54) * mm, v(10.39, 0) * mm], "startDerivative": vector(-0.27, 5.72) * mm, "endDerivative": vector(-7.33, 5.7) * mm});
            skLineSegment(sketch, "E367.MirrorCS", {"start": v(18.08, -1.9) * mm, "end": v(17.56, 0) * mm});
            skLineSegment(sketch, "E368.MirrorCS", {"start": v(23.53, -1.42) * mm, "end": v(20.25, -1.35) * mm});
            skFitSpline(sketch, "E369.MirrorCS", {"points": [v(41.07, -23.71) * mm, v(43.34, -14.1) * mm, v(36.97, -5.76) * mm, v(25.25, -1.72) * mm], "startDerivative": vector(20.23, 34.33) * mm, "endDerivative": vector(-34.18, 6.94) * mm});
            skLineSegment(sketch, "E370.MirrorCS", {"start": v(20.25, -1.35) * mm, "end": v(19.93, -1.9) * mm});
            skLineSegment(sketch, "E371.MirrorCS", {"start": v(16.35, 0) * mm, "end": v(16.98, -1.85) * mm});
            skLineSegment(sketch, "E372.MirrorCS", {"start": v(3.77, 0) * mm, "end": v(2.83, -1.63) * mm});
            skLineSegment(sketch, "E373.MirrorCS", {"start": v(5.78, -1.25) * mm, "end": v(10.45, -2.5) * mm});
            skLineSegment(sketch, "E374.MirrorCS", {"start": v(4.88, -2.81) * mm, "end": v(5.78, -1.25) * mm});
            skCircle(sketch, "E375", {"center": v(0, 0) * mm, "radius": 47.25 * mm});
            skCircle(sketch, "E376", {"center": v(0, 0) * mm, "radius": 50 * mm});
            skSolve(sketch);
        }
        {
            var Q0;
            Q0=makeQuery(id+"F0.imprint","IMPRINT",FACE,{"disambiguationData":[TD([[makeQuery(id+"F0.imprint","IMPRINT",EDGE,{"derivedFrom":sQuery(id+"F0.wireOp",EDGE,"E126.MirrorCS")}),-1.0]])]});
            var Q1;
            Q1=makeQuery(id+"F0.imprint","IMPRINT",FACE,{"disambiguationData":[TD([[makeQuery(id+"F0.imprint","IMPRINT",EDGE,{"derivedFrom":sQuery(id+"F0.wireOp",EDGE,"E131.MirrorCS")}),1.0]])]});
            var Q2;
            {var subQ1=sQuery(id+"F0.wireOp",EDGE,"E1.3.0");var subQ5=sQuery(id+"F0.wireOp",EDGE,"E376");var subQ6=makeQuery(id+"F0.imprint","INTERSECT",VERTEX,{"derivedFrom":[subQ1,subQ5]});Q2=makeQuery(id+"F0.imprint","IMPRINT",FACE,{"disambiguationData":[TD([[makeQuery(id+"F0.imprint","IMPRINT",EDGE,{"disambiguationData":[TD([[subQ6,1.0]])],"derivedFrom":subQ1}),-1.0]])]});}
            var Q3;
            {var subQ1=sQuery(id+"F0.wireOp",EDGE,"E1.2.0");var subQ3=sQuery(id+"F0.wireOp",EDGE,"E375");var subQ4=makeQuery(id+"F0.imprint","INTERSECT",VERTEX,{"derivedFrom":[subQ1,subQ3]});Q3=makeQuery(id+"F0.imprint","IMPRINT",FACE,{"disambiguationData":[TD([[makeQuery(id+"F0.imprint","IMPRINT",EDGE,{"disambiguationData":[TD([[subQ4,-1.0]])],"derivedFrom":subQ3}),-1.0]])]});}
            var Q4;
            {var subQ1=sQuery(id+"F0.wireOp",EDGE,"E1.2.0");var subQ3=sQuery(id+"F0.wireOp",EDGE,"E375");var subQ4=makeQuery(id+"F0.imprint","INTERSECT",VERTEX,{"derivedFrom":[subQ1,subQ3]});Q4=makeQuery(id+"F0.imprint","IMPRINT",FACE,{"disambiguationData":[TD([[makeQuery(id+"F0.imprint","IMPRINT",EDGE,{"disambiguationData":[TD([[subQ4,1.0]])],"derivedFrom":subQ3}),-1.0]])]});}
            var Q5;
            {var subQ1=sQuery(id+"F0.wireOp",EDGE,"E1.1.0");var subQ5=sQuery(id+"F0.wireOp",EDGE,"E376");var subQ9=makeQuery(id+"F0.imprint","INTERSECT",VERTEX,{"derivedFrom":[subQ1,subQ5]});Q5=makeQuery(id+"F0.imprint","IMPRINT",FACE,{"disambiguationData":[TD([[makeQuery(id+"F0.imprint","IMPRINT",EDGE,{"disambiguationData":[TD([[subQ9,1.0]])],"derivedFrom":subQ1}),1.0]])]});}
            var Q6;
            {var subQ14=sQuery(id+"F0.wireOp",EDGE,"E3");Q6=makeQuery(id+"F0.imprint","IMPRINT",FACE,{"disambiguationData":[TD([[makeQuery(id+"F0.imprint","IMPRINT",EDGE,{"derivedFrom":subQ14}),1.0]])]});}
            var Q7;
            Q7=makeQuery(id+"F0.imprint","IMPRINT",FACE,{"disambiguationData":[TD([[makeQuery(id+"F0.imprint","IMPRINT",EDGE,{"derivedFrom":sQuery(id+"F0.wireOp",EDGE,"E33.MirrorCS")}),-1.0]])]});
            var Q8;
            Q8=makeQuery(id+"F0.imprint","IMPRINT",FACE,{"disambiguationData":[TD([[makeQuery(id+"F0.imprint","IMPRINT",EDGE,{"derivedFrom":sQuery(id+"F0.wireOp",EDGE,"E65.MirrorCS")}),1.0]])]});
            var Q9;
            Q9=makeQuery(id+"F0.imprint","IMPRINT",FACE,{"disambiguationData":[TD([[makeQuery(id+"F0.imprint","IMPRINT",EDGE,{"derivedFrom":sQuery(id+"F0.wireOp",EDGE,"E64.MirrorCS")}),-1.0]])]});
            var Q10;
            Q10=makeQuery(id+"F0.imprint","IMPRINT",FACE,{"disambiguationData":[TD([[makeQuery(id+"F0.imprint","IMPRINT",EDGE,{"derivedFrom":sQuery(id+"F0.wireOp",EDGE,"E250.MirrorCS")}),1.0]])]});
            var Q11;
            Q11=makeQuery(id+"F0.imprint","IMPRINT",FACE,{"disambiguationData":[TD([[makeQuery(id+"F0.imprint","IMPRINT",EDGE,{"derivedFrom":sQuery(id+"F0.wireOp",EDGE,"E251.MirrorCS")}),-1.0]])]});
            var Q12;
            {var subQ10=sQuery(id+"F0.wireOp",EDGE,"E257.MirrorCS");Q12=makeQuery(id+"F0.imprint","IMPRINT",FACE,{"disambiguationData":[TD([[makeQuery(id+"F0.imprint","IMPRINT",EDGE,{"derivedFrom":subQ10}),1.0]])]});}
            var Q13;
            Q13=makeQuery(id+"F0.imprint","IMPRINT",FACE,{"disambiguationData":[TD([[makeQuery(id+"F0.imprint","IMPRINT",EDGE,{"derivedFrom":sQuery(id+"F0.wireOp",EDGE,"E253.MirrorCS")}),1.0]])]});
            var Q14;
            {var subQ14=sQuery(id+"F0.wireOp",EDGE,"E143.MirrorCS");Q14=makeQuery(id+"F0.imprint","IMPRINT",FACE,{"disambiguationData":[TD([[makeQuery(id+"F0.imprint","IMPRINT",EDGE,{"derivedFrom":subQ14}),1.0]])]});}
            var Q15;
            Q15=makeQuery(id+"F0.imprint","IMPRINT",FACE,{"disambiguationData":[TD([[makeQuery(id+"F0.imprint","IMPRINT",EDGE,{"derivedFrom":sQuery(id+"F0.wireOp",EDGE,"E127.MirrorCS")}),-1.0]])]});
            var Q16;
            {var subQ0=sQuery(id+"F0.wireOp",EDGE,"E376");var subQ1=sQuery(id+"F0.wireOp",EDGE,"E1.3.0");var subQ2=makeQuery(id+"F0.imprint","INTERSECT",VERTEX,{"derivedFrom":[subQ1,subQ0]});Q16=makeQuery(id+"F0.imprint","IMPRINT",FACE,{"disambiguationData":[TD([[makeQuery(id+"F0.imprint","IMPRINT",EDGE,{"disambiguationData":[TD([[subQ2,1.0]])],"derivedFrom":subQ1}),1.0]])]});}
            var Q17;
            {var subQ1=sQuery(id+"F0.wireOp",EDGE,"E1.4.0");var subQ3=sQuery(id+"F0.wireOp",EDGE,"E375");var subQ4=makeQuery(id+"F0.imprint","INTERSECT",VERTEX,{"derivedFrom":[subQ1,subQ3]});Q17=makeQuery(id+"F0.imprint","IMPRINT",FACE,{"disambiguationData":[TD([[makeQuery(id+"F0.imprint","IMPRINT",EDGE,{"disambiguationData":[TD([[subQ4,-1.0]])],"derivedFrom":subQ3}),-1.0]])]});}
            var Q18;
            {var subQ1=sQuery(id+"F0.wireOp",EDGE,"E1.4.0");var subQ3=sQuery(id+"F0.wireOp",EDGE,"E375");var subQ4=makeQuery(id+"F0.imprint","INTERSECT",VERTEX,{"derivedFrom":[subQ1,subQ3]});Q18=makeQuery(id+"F0.imprint","IMPRINT",FACE,{"disambiguationData":[TD([[makeQuery(id+"F0.imprint","IMPRINT",EDGE,{"disambiguationData":[TD([[subQ4,1.0]])],"derivedFrom":subQ3}),-1.0]])]});}
            var Q19;
            {var subQ1=sQuery(id+"F0.wireOp",EDGE,"E1.5.0");var subQ7=sQuery(id+"F0.wireOp",EDGE,"E376");var subQ8=makeQuery(id+"F0.imprint","INTERSECT",VERTEX,{"derivedFrom":[subQ1,subQ7]});Q19=makeQuery(id+"F0.imprint","IMPRINT",FACE,{"disambiguationData":[TD([[makeQuery(id+"F0.imprint","IMPRINT",EDGE,{"disambiguationData":[TD([[subQ8,1.0]])],"derivedFrom":subQ1}),-1.0]])]});}
            var Q20;
            {var subQ1=sQuery(id+"F0.wireOp",EDGE,"E1.1.0");var subQ7=sQuery(id+"F0.wireOp",EDGE,"E376");var subQ8=makeQuery(id+"F0.imprint","INTERSECT",VERTEX,{"derivedFrom":[subQ1,subQ7]});Q20=makeQuery(id+"F0.imprint","IMPRINT",FACE,{"disambiguationData":[TD([[makeQuery(id+"F0.imprint","IMPRINT",EDGE,{"disambiguationData":[TD([[subQ8,1.0]])],"derivedFrom":subQ1}),-1.0]])]});}
            var Q21;
            {var subQ1=sQuery(id+"F0.wireOp",EDGE,"E0");var subQ3=sQuery(id+"F0.wireOp",EDGE,"E375");var subQ4=makeQuery(id+"F0.imprint","INTERSECT",VERTEX,{"derivedFrom":[subQ1,subQ3]});Q21=makeQuery(id+"F0.imprint","IMPRINT",FACE,{"disambiguationData":[TD([[makeQuery(id+"F0.imprint","IMPRINT",EDGE,{"disambiguationData":[TD([[subQ4,-1.0]])],"derivedFrom":subQ3}),-1.0]])]});}
            var Q22;
            {var subQ1=sQuery(id+"F0.wireOp",EDGE,"E1.11.0");var subQ5=sQuery(id+"F0.wireOp",EDGE,"E376");var subQ8=makeQuery(id+"F0.imprint","INTERSECT",VERTEX,{"derivedFrom":[subQ1,subQ5]});Q22=makeQuery(id+"F0.imprint","IMPRINT",FACE,{"disambiguationData":[TD([[makeQuery(id+"F0.imprint","IMPRINT",EDGE,{"disambiguationData":[TD([[subQ8,1.0]])],"derivedFrom":subQ1}),1.0]])]});}
            var Q23;
            {var subQ1=sQuery(id+"F0.wireOp",EDGE,"E0");var subQ3=sQuery(id+"F0.wireOp",EDGE,"E375");var subQ4=makeQuery(id+"F0.imprint","INTERSECT",VERTEX,{"derivedFrom":[subQ1,subQ3]});Q23=makeQuery(id+"F0.imprint","IMPRINT",FACE,{"disambiguationData":[TD([[makeQuery(id+"F0.imprint","IMPRINT",EDGE,{"disambiguationData":[TD([[subQ4,1.0]])],"derivedFrom":subQ3}),-1.0]])]});}
            var Q24;
            {var subQ1=sQuery(id+"F0.wireOp",EDGE,"E1.11.0");var subQ5=sQuery(id+"F0.wireOp",EDGE,"E376");var subQ8=makeQuery(id+"F0.imprint","INTERSECT",VERTEX,{"derivedFrom":[subQ1,subQ5]});Q24=makeQuery(id+"F0.imprint","IMPRINT",FACE,{"disambiguationData":[TD([[makeQuery(id+"F0.imprint","IMPRINT",EDGE,{"disambiguationData":[TD([[subQ8,1.0]])],"derivedFrom":subQ1}),-1.0]])]});}
            var Q25;
            {var subQ1=sQuery(id+"F0.wireOp",EDGE,"E1.10.0");var subQ3=sQuery(id+"F0.wireOp",EDGE,"E375");var subQ4=makeQuery(id+"F0.imprint","INTERSECT",VERTEX,{"derivedFrom":[subQ1,subQ3]});Q25=makeQuery(id+"F0.imprint","IMPRINT",FACE,{"disambiguationData":[TD([[makeQuery(id+"F0.imprint","IMPRINT",EDGE,{"disambiguationData":[TD([[subQ4,-1.0]])],"derivedFrom":subQ3}),-1.0]])]});}
            var Q26;
            {var subQ1=sQuery(id+"F0.wireOp",EDGE,"E1.10.0");var subQ3=sQuery(id+"F0.wireOp",EDGE,"E375");var subQ4=makeQuery(id+"F0.imprint","INTERSECT",VERTEX,{"derivedFrom":[subQ1,subQ3]});Q26=makeQuery(id+"F0.imprint","IMPRINT",FACE,{"disambiguationData":[TD([[makeQuery(id+"F0.imprint","IMPRINT",EDGE,{"disambiguationData":[TD([[subQ4,1.0]])],"derivedFrom":subQ3}),-1.0]])]});}
            var Q27;
            {var subQ5=sQuery(id+"F0.wireOp",EDGE,"E376");var subQ6=sQuery(id+"F0.wireOp",EDGE,"E1.9.0");var subQ7=makeQuery(id+"F0.imprint","INTERSECT",VERTEX,{"derivedFrom":[subQ6,subQ5]});Q27=makeQuery(id+"F0.imprint","IMPRINT",FACE,{"disambiguationData":[TD([[makeQuery(id+"F0.imprint","IMPRINT",EDGE,{"disambiguationData":[TD([[subQ7,1.0]])],"derivedFrom":subQ6}),1.0]])]});}
            var Q28;
            {var subQ1=sQuery(id+"F0.wireOp",EDGE,"E1.9.0");var subQ5=sQuery(id+"F0.wireOp",EDGE,"E376");var subQ6=makeQuery(id+"F0.imprint","INTERSECT",VERTEX,{"derivedFrom":[subQ1,subQ5]});Q28=makeQuery(id+"F0.imprint","IMPRINT",FACE,{"disambiguationData":[TD([[makeQuery(id+"F0.imprint","IMPRINT",EDGE,{"disambiguationData":[TD([[subQ6,1.0]])],"derivedFrom":subQ1}),-1.0]])]});}
            var Q29;
            {var subQ1=sQuery(id+"F0.wireOp",EDGE,"E1.8.0");var subQ3=sQuery(id+"F0.wireOp",EDGE,"E375");var subQ4=makeQuery(id+"F0.imprint","INTERSECT",VERTEX,{"derivedFrom":[subQ1,subQ3]});Q29=makeQuery(id+"F0.imprint","IMPRINT",FACE,{"disambiguationData":[TD([[makeQuery(id+"F0.imprint","IMPRINT",EDGE,{"disambiguationData":[TD([[subQ4,1.0]])],"derivedFrom":subQ3}),-1.0]])]});}
            var Q30;
            {var subQ1=sQuery(id+"F0.wireOp",EDGE,"E1.8.0");var subQ3=sQuery(id+"F0.wireOp",EDGE,"E375");var subQ4=makeQuery(id+"F0.imprint","INTERSECT",VERTEX,{"derivedFrom":[subQ1,subQ3]});Q30=makeQuery(id+"F0.imprint","IMPRINT",FACE,{"disambiguationData":[TD([[makeQuery(id+"F0.imprint","IMPRINT",EDGE,{"disambiguationData":[TD([[subQ4,-1.0]])],"derivedFrom":subQ3}),-1.0]])]});}
            var Q31;
            {var subQ1=sQuery(id+"F0.wireOp",EDGE,"E1.7.0");var subQ7=sQuery(id+"F0.wireOp",EDGE,"E376");var subQ9=makeQuery(id+"F0.imprint","INTERSECT",VERTEX,{"derivedFrom":[subQ1,subQ7]});Q31=makeQuery(id+"F0.imprint","IMPRINT",FACE,{"disambiguationData":[TD([[makeQuery(id+"F0.imprint","IMPRINT",EDGE,{"disambiguationData":[TD([[subQ9,1.0]])],"derivedFrom":subQ1}),1.0]])]});}
            var Q32;
            {var subQ5=sQuery(id+"F0.wireOp",EDGE,"E1.7.0");var subQ7=sQuery(id+"F0.wireOp",EDGE,"E376");var subQ8=makeQuery(id+"F0.imprint","INTERSECT",VERTEX,{"derivedFrom":[subQ5,subQ7]});Q32=makeQuery(id+"F0.imprint","IMPRINT",FACE,{"disambiguationData":[TD([[makeQuery(id+"F0.imprint","IMPRINT",EDGE,{"disambiguationData":[TD([[subQ8,1.0]])],"derivedFrom":subQ5}),-1.0]])]});}
            var Q33;
            {var subQ1=sQuery(id+"F0.wireOp",EDGE,"E1.6.0");var subQ3=sQuery(id+"F0.wireOp",EDGE,"E375");var subQ4=makeQuery(id+"F0.imprint","INTERSECT",VERTEX,{"derivedFrom":[subQ1,subQ3]});Q33=makeQuery(id+"F0.imprint","IMPRINT",FACE,{"disambiguationData":[TD([[makeQuery(id+"F0.imprint","IMPRINT",EDGE,{"disambiguationData":[TD([[subQ4,-1.0]])],"derivedFrom":subQ3}),-1.0]])]});}
            var Q34;
            {var subQ1=sQuery(id+"F0.wireOp",EDGE,"E1.6.0");var subQ3=sQuery(id+"F0.wireOp",EDGE,"E375");var subQ4=makeQuery(id+"F0.imprint","INTERSECT",VERTEX,{"derivedFrom":[subQ1,subQ3]});Q34=makeQuery(id+"F0.imprint","IMPRINT",FACE,{"disambiguationData":[TD([[makeQuery(id+"F0.imprint","IMPRINT",EDGE,{"disambiguationData":[TD([[subQ4,1.0]])],"derivedFrom":subQ3}),-1.0]])]});}
            var Q35;
            {var subQ1=sQuery(id+"F0.wireOp",EDGE,"E1.5.0");var subQ7=sQuery(id+"F0.wireOp",EDGE,"E376");var subQ9=makeQuery(id+"F0.imprint","INTERSECT",VERTEX,{"derivedFrom":[subQ1,subQ7]});Q35=makeQuery(id+"F0.imprint","IMPRINT",FACE,{"disambiguationData":[TD([[makeQuery(id+"F0.imprint","IMPRINT",EDGE,{"disambiguationData":[TD([[subQ9,1.0]])],"derivedFrom":subQ1}),1.0]])]});}
            extrude(context, id + "F1", {"entities" : qUnion([Q0, Q1, Q2, Q3, Q4, Q5, Q6, Q7, Q8, Q9, Q10, Q11, Q12, Q13, Q14, Q15, Q16, Q17, Q18, Q19, Q20, Q21, Q22, Q23, Q24, Q25, Q26, Q27, Q28, Q29, Q30, Q31, Q32, Q33, Q34, Q35]), "depth" : 5 * mm, "offsetDistance" : 25 * mm});
        }
    });
